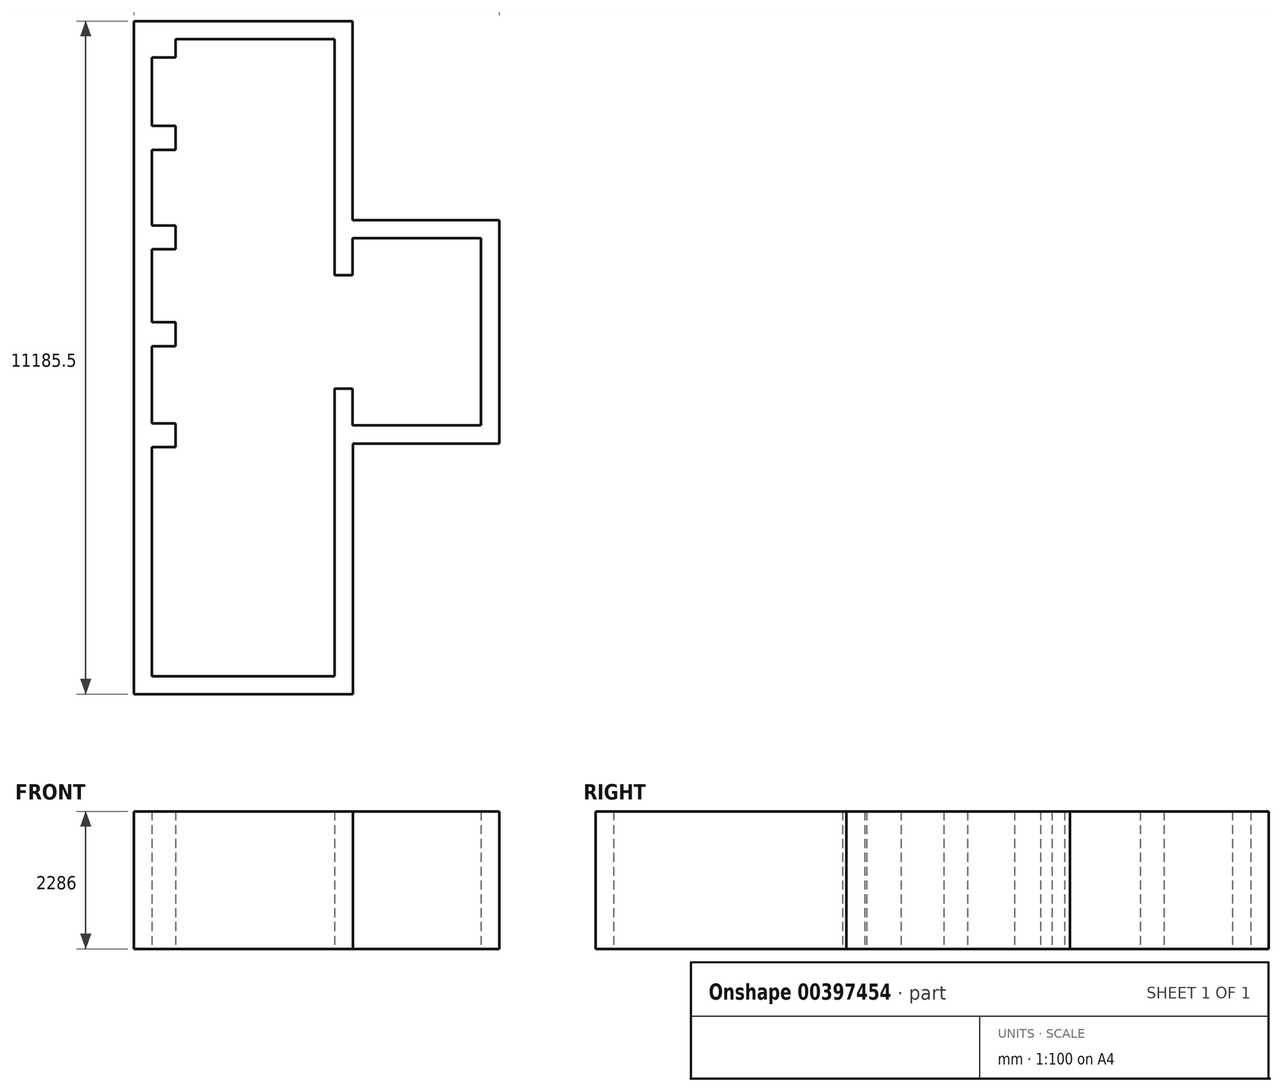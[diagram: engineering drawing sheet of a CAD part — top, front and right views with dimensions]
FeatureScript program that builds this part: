
annotation { "Feature Type Name" : "Feature", "Feature Type Description" : "" }
export const myFeature = defineFeature(function(context is Context, id is Id, definition is map)
    precondition{}
    {
        {
            var Q0;
            Q0=qCreatedBy(makeId("Top.planeOp"),FACE);
            var sketch = newSketch(context, id + "F0", { "sketchPlane" : qUnion([Q0])});
            skLineSegment(sketch, "E0", {"start": v(0, 0) * mm, "end": v(-2641.6, 0) * mm});
            skLineSegment(sketch, "E1", {"start": v(0, 0) * mm, "end": v(0, -3924.3) * mm});
            skLineSegment(sketch, "E2", {"start": v(0, -3924.3) * mm, "end": v(295.28, -3924.3) * mm});
            skLineSegment(sketch, "E3", {"start": v(295.28, -3924.3) * mm, "end": v(295.28, -3305.17) * mm});
            skLineSegment(sketch, "E4", {"start": v(295.28, -3305.17) * mm, "end": v(2428.88, -3305.17) * mm});
            skLineSegment(sketch, "E5", {"start": v(2428.88, -3305.17) * mm, "end": v(2428.88, -6416.67) * mm});
            skLineSegment(sketch, "E6", {"start": v(2428.88, -6416.67) * mm, "end": v(295.28, -6416.67) * mm});
            skLineSegment(sketch, "E7", {"start": v(295.28, -6416.67) * mm, "end": v(295.28, -5810.25) * mm});
            skLineSegment(sketch, "E8", {"start": v(295.28, -5810.25) * mm, "end": v(0, -5810.25) * mm});
            skLineSegment(sketch, "E9", {"start": v(0, -5810.25) * mm, "end": v(0, -10588.62) * mm});
            skLineSegment(sketch, "E10", {"start": v(-2641.6, 0) * mm, "end": v(-2641.6, -304.8) * mm});
            skLineSegment(sketch, "E11", {"start": v(-2641.6, -304.8) * mm, "end": v(-3038.47, -304.8) * mm});
            skLineSegment(sketch, "E12", {"start": v(-3038.47, -304.8) * mm, "end": v(-3038.47, -1441.45) * mm});
            skLineSegment(sketch, "E13", {"start": v(-3038.47, -1441.45) * mm, "end": v(-2641.6, -1441.45) * mm});
            skLineSegment(sketch, "E14", {"start": v(-2641.6, -1441.45) * mm, "end": v(-2641.6, -1838.33) * mm});
            skLineSegment(sketch, "E15", {"start": v(-2641.6, -1838.33) * mm, "end": v(-3038.47, -1838.33) * mm});
            skLineSegment(sketch, "E16", {"start": v(-3038.47, -1838.33) * mm, "end": v(-3038.47, -3097.21) * mm});
            skLineSegment(sketch, "E17", {"start": v(-3038.47, -3097.21) * mm, "end": v(-2641.6, -3097.21) * mm});
            skLineSegment(sketch, "E18", {"start": v(-2641.6, -3097.21) * mm, "end": v(-2641.6, -3494.09) * mm});
            skLineSegment(sketch, "E19", {"start": v(-2641.6, -3494.09) * mm, "end": v(-3038.47, -3494.09) * mm});
            skLineSegment(sketch, "E20", {"start": v(-3038.47, -3494.09) * mm, "end": v(-3038.47, -4705.35) * mm});
            skLineSegment(sketch, "E21", {"start": v(-3038.47, -4705.35) * mm, "end": v(-2641.6, -4705.35) * mm});
            skLineSegment(sketch, "E22", {"start": v(-2641.6, -4705.35) * mm, "end": v(-2641.6, -5102.23) * mm});
            skLineSegment(sketch, "E23", {"start": v(-2641.6, -5102.23) * mm, "end": v(-3038.47, -5102.23) * mm});
            skLineSegment(sketch, "E24", {"start": v(-3038.47, -5102.23) * mm, "end": v(-3038.47, -6386.51) * mm});
            skLineSegment(sketch, "E25", {"start": v(-3038.47, -6386.51) * mm, "end": v(-2641.6, -6386.51) * mm});
            skLineSegment(sketch, "E26", {"start": v(-2641.6, -6386.51) * mm, "end": v(-2641.6, -6783.39) * mm});
            skLineSegment(sketch, "E27", {"start": v(-2641.6, -6783.39) * mm, "end": v(-3038.47, -6783.39) * mm});
            skLineSegment(sketch, "E28", {"start": v(-3038.47, -6783.39) * mm, "end": v(-3038.47, -10588.62) * mm});
            skLineSegment(sketch, "E29", {"start": v(-3038.47, -10588.62) * mm, "end": v(0, -10588.62) * mm});
            skLineSegment(sketch, "E30.0", {"start": v(301.63, -3930.65) * mm, "end": v(301.63, -3311.52) * mm});
            skLineSegment(sketch, "E30.1", {"start": v(-6.35, -3930.65) * mm, "end": v(301.63, -3930.65) * mm});
            skLineSegment(sketch, "E30.2", {"start": v(-6.35, -6.35) * mm, "end": v(-6.35, -3930.65) * mm});
            skLineSegment(sketch, "E30.3", {"start": v(-6.35, -6.35) * mm, "end": v(-2635.25, -6.35) * mm});
            skLineSegment(sketch, "E30.4", {"start": v(-2635.25, -6.35) * mm, "end": v(-2635.25, -311.15) * mm});
            skLineSegment(sketch, "E30.5", {"start": v(-2635.25, -311.15) * mm, "end": v(-3032.12, -311.15) * mm});
            skLineSegment(sketch, "E30.6", {"start": v(-3032.12, -311.15) * mm, "end": v(-3032.12, -1435.1) * mm});
            skLineSegment(sketch, "E30.7", {"start": v(-3032.12, -6380.16) * mm, "end": v(-2635.25, -6380.16) * mm});
            skLineSegment(sketch, "E30.8", {"start": v(-2635.25, -6380.16) * mm, "end": v(-2635.25, -6789.74) * mm});
            skLineSegment(sketch, "E30.9", {"start": v(-2635.25, -6789.74) * mm, "end": v(-3032.12, -6789.74) * mm});
            skLineSegment(sketch, "E30.10", {"start": v(-3032.12, -6789.74) * mm, "end": v(-3032.12, -10582.28) * mm});
            skLineSegment(sketch, "E30.11", {"start": v(-3032.12, -10582.28) * mm, "end": v(-6.35, -10582.28) * mm});
            skLineSegment(sketch, "E30.12", {"start": v(-6.35, -5803.9) * mm, "end": v(-6.35, -10582.28) * mm});
            skLineSegment(sketch, "E30.13", {"start": v(2422.53, -3311.52) * mm, "end": v(2422.53, -6410.32) * mm});
            skLineSegment(sketch, "E30.14", {"start": v(2422.53, -6410.32) * mm, "end": v(301.63, -6410.32) * mm});
            skLineSegment(sketch, "E30.15", {"start": v(301.63, -6410.32) * mm, "end": v(301.63, -5803.9) * mm});
            skLineSegment(sketch, "E30.16", {"start": v(301.63, -5803.9) * mm, "end": v(-6.35, -5803.9) * mm});
            skLineSegment(sketch, "E30.17", {"start": v(-3032.12, -5108.58) * mm, "end": v(-3032.12, -6380.16) * mm});
            skLineSegment(sketch, "E30.18", {"start": v(-2635.25, -5108.58) * mm, "end": v(-3032.12, -5108.58) * mm});
            skLineSegment(sketch, "E30.19", {"start": v(-2635.25, -4699) * mm, "end": v(-2635.25, -5108.58) * mm});
            skLineSegment(sketch, "E30.20", {"start": v(-3032.12, -4699) * mm, "end": v(-2635.25, -4699) * mm});
            skLineSegment(sketch, "E30.21", {"start": v(-3032.12, -3500.44) * mm, "end": v(-3032.12, -4699) * mm});
            skLineSegment(sketch, "E30.22", {"start": v(-2635.25, -3500.44) * mm, "end": v(-3032.12, -3500.44) * mm});
            skLineSegment(sketch, "E30.23", {"start": v(-2635.25, -3090.86) * mm, "end": v(-2635.25, -3500.44) * mm});
            skLineSegment(sketch, "E30.24", {"start": v(301.63, -3311.52) * mm, "end": v(2422.53, -3311.52) * mm});
            skLineSegment(sketch, "E30.25", {"start": v(-3032.12, -3090.86) * mm, "end": v(-2635.25, -3090.86) * mm});
            skLineSegment(sketch, "E30.26", {"start": v(-3032.12, -1844.68) * mm, "end": v(-3032.12, -3090.86) * mm});
            skLineSegment(sketch, "E30.27", {"start": v(-2635.25, -1844.68) * mm, "end": v(-3032.12, -1844.68) * mm});
            skLineSegment(sketch, "E30.28", {"start": v(-2635.25, -1435.1) * mm, "end": v(-2635.25, -1844.68) * mm});
            skLineSegment(sketch, "E30.29", {"start": v(-3032.12, -1435.1) * mm, "end": v(-2635.25, -1435.1) * mm});
            skLineSegment(sketch, "E31", {"start": v(-3336.92, 298.45) * mm, "end": v(-3336.92, -10887.08) * mm});
            skLineSegment(sketch, "E32", {"start": v(-3336.92, -10887.08) * mm, "end": v(304.8, -10887.08) * mm});
            skLineSegment(sketch, "E33", {"start": v(304.8, -10887.08) * mm, "end": v(304.8, -6721.48) * mm});
            skLineSegment(sketch, "E34", {"start": v(304.8, -6721.48) * mm, "end": v(2733.68, -6721.47) * mm});
            skLineSegment(sketch, "E35", {"start": v(2733.68, -6721.47) * mm, "end": v(2733.68, -3006.72) * mm});
            skLineSegment(sketch, "E36", {"start": v(2733.68, -3006.72) * mm, "end": v(298.45, -3006.72) * mm});
            skLineSegment(sketch, "E37", {"start": v(298.45, -3006.72) * mm, "end": v(298.45, 298.45) * mm});
            skLineSegment(sketch, "E38", {"start": v(298.45, 298.45) * mm, "end": v(-3336.92, 298.45) * mm});
            skSolve(sketch);
        }
        {
            var Q0;
            Q0 = qSketchRegion(id + "F0", true);
            extrude(context, id + "F1", {"entities" : qUnion([Q0]), "depth" : 2286 * mm});
        }
    });
